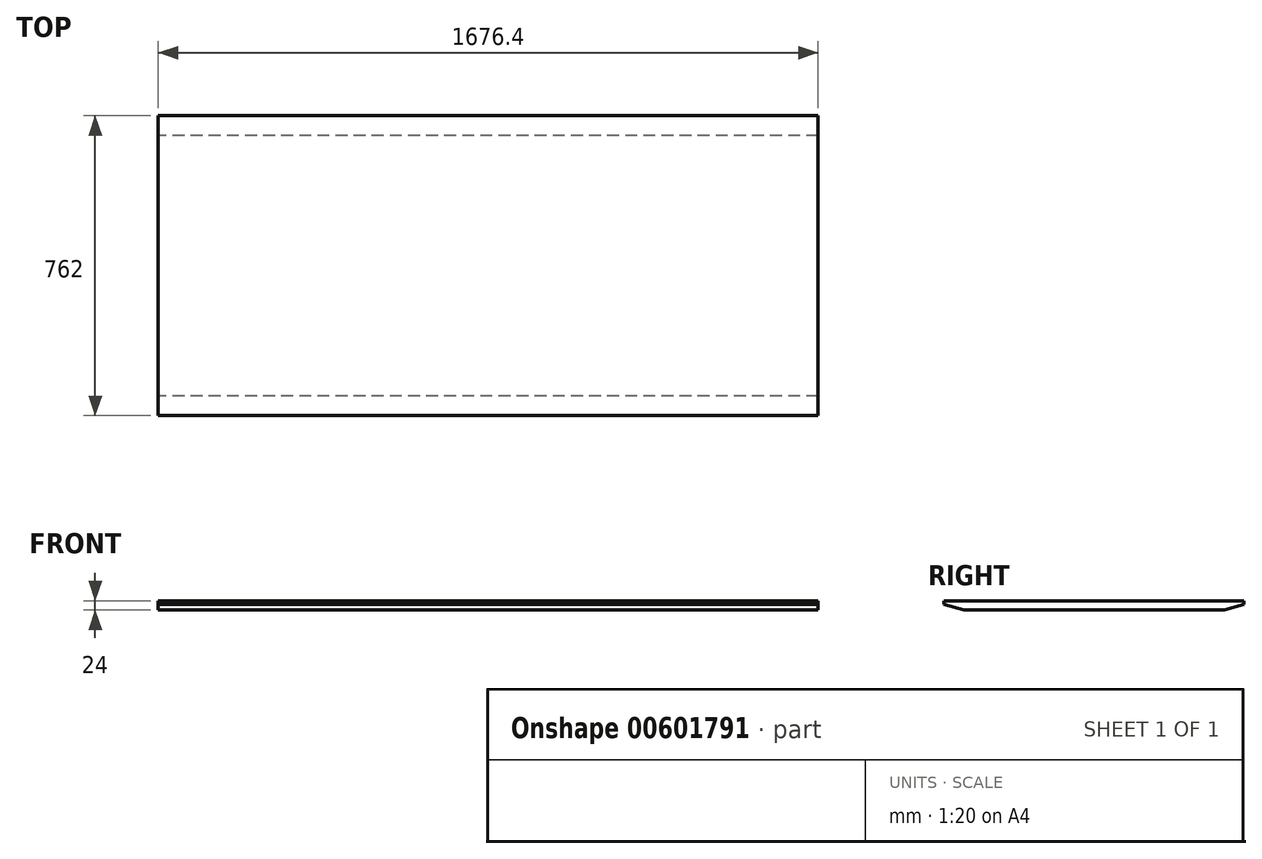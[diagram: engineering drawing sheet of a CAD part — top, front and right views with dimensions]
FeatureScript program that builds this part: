
annotation { "Feature Type Name" : "Feature", "Feature Type Description" : "" }
export const myFeature = defineFeature(function(context is Context, id is Id, definition is map)
    precondition{}
    {
        {
            var Q0;
            Q0=qCreatedBy(makeId("Top.planeOp"),FACE);
            var sketch = newSketch(context, id + "F0", { "sketchPlane" : qUnion([Q0])});
            skLineSegment(sketch, "E0.bottom", {"start": v(838.2, 381) * mm, "end": v(-838.2, 381) * mm});
            skLineSegment(sketch, "E0.top", {"start": v(838.2, -381) * mm, "end": v(-838.2, -381) * mm});
            skLineSegment(sketch, "E0.left", {"start": v(838.2, 381) * mm, "end": v(838.2, -381) * mm});
            skLineSegment(sketch, "E0.right", {"start": v(-838.2, 381) * mm, "end": v(-838.2, -381) * mm});
            skPoint(sketch, "E0.middle", {"position": v(0, 0) * mm});
            skSolve(sketch);
        }
        {
            var Q0;
            Q0=qSketchRegion(id+"F0",true);
            extrude(context, id + "F1", {"entities" : qUnion([Q0]), "depth" : 24 * mm, "offsetDistance" : 25.4 * mm});
        }
        {
            var Q0;
            Q0=makeQuery(id+"F1.opExtrude","SWEPT_FACE",FACE,{"disambiguationData":[OSD([sQuery(id+"F0.wireOp",EDGE,"E0.left")])]});
            var sketch = newSketch(context, id + "F2", { "sketchPlane" : qUnion([Q0])});
            skLineSegment(sketch, "E1", {"start": v(331, 0) * mm, "end": v(381, 14) * mm});
            skLineSegment(sketch, "E2", {"start": v(381, 14) * mm, "end": v(381, 0) * mm});
            skLineSegment(sketch, "E3", {"start": v(381, 0) * mm, "end": v(331, 0) * mm});
            skLineSegment(sketch, "E4", {"start": v(0, 0) * mm, "end": v(0, 154.27) * mm, "construction": true});
            skPoint(sketch, "E4.endSnap0", {"position": v(0, 24) * mm});
            skLineSegment(sketch, "E5.MirrorCS", {"start": v(-331, 0) * mm, "end": v(-381, 14) * mm});
            skLineSegment(sketch, "E6.MirrorCS", {"start": v(-381, 14) * mm, "end": v(-381, 0) * mm});
            skLineSegment(sketch, "E7.MirrorCS", {"start": v(-381, 0) * mm, "end": v(-331, 0) * mm});
            skSolve(sketch);
        }
        {
            var Q0;
            Q0=makeQuery(id+"F1.opExtrude","CAP_FACE",FACE,{"disambiguationData":[OSD([sQuery(id+"F0.wireOp",EDGE,"E0.bottom"),sQuery(id+"F0.wireOp",EDGE,"E0.top"),sQuery(id+"F0.wireOp",EDGE,"E0.left"),sQuery(id+"F0.wireOp",EDGE,"E0.right")])],"isStart":true});
            var sketch = newSketch(context, id + "F3", { "sketchPlane" : qUnion([Q0])});
            skLineSegment(sketch, "E8", {"start": v(-838.2, 381) * mm, "end": v(838.2, 381) * mm});
            skLineSegment(sketch, "E9", {"start": v(-838.2, -381) * mm, "end": v(838.2, -381) * mm});
            skSolve(sketch);
        }
        {
            var Q0;
            Q0 = qSketchRegion(id + "F2", true);
            var Q1;
            Q1=sQuery(id+"F3.wireOp",EDGE,"E8");
            sweep(context, id + "F4", {"operationType" : NewBodyOperationType.REMOVE, "profiles" : qUnion([Q0]), "path" : qUnion([Q1])});
        }
    });
